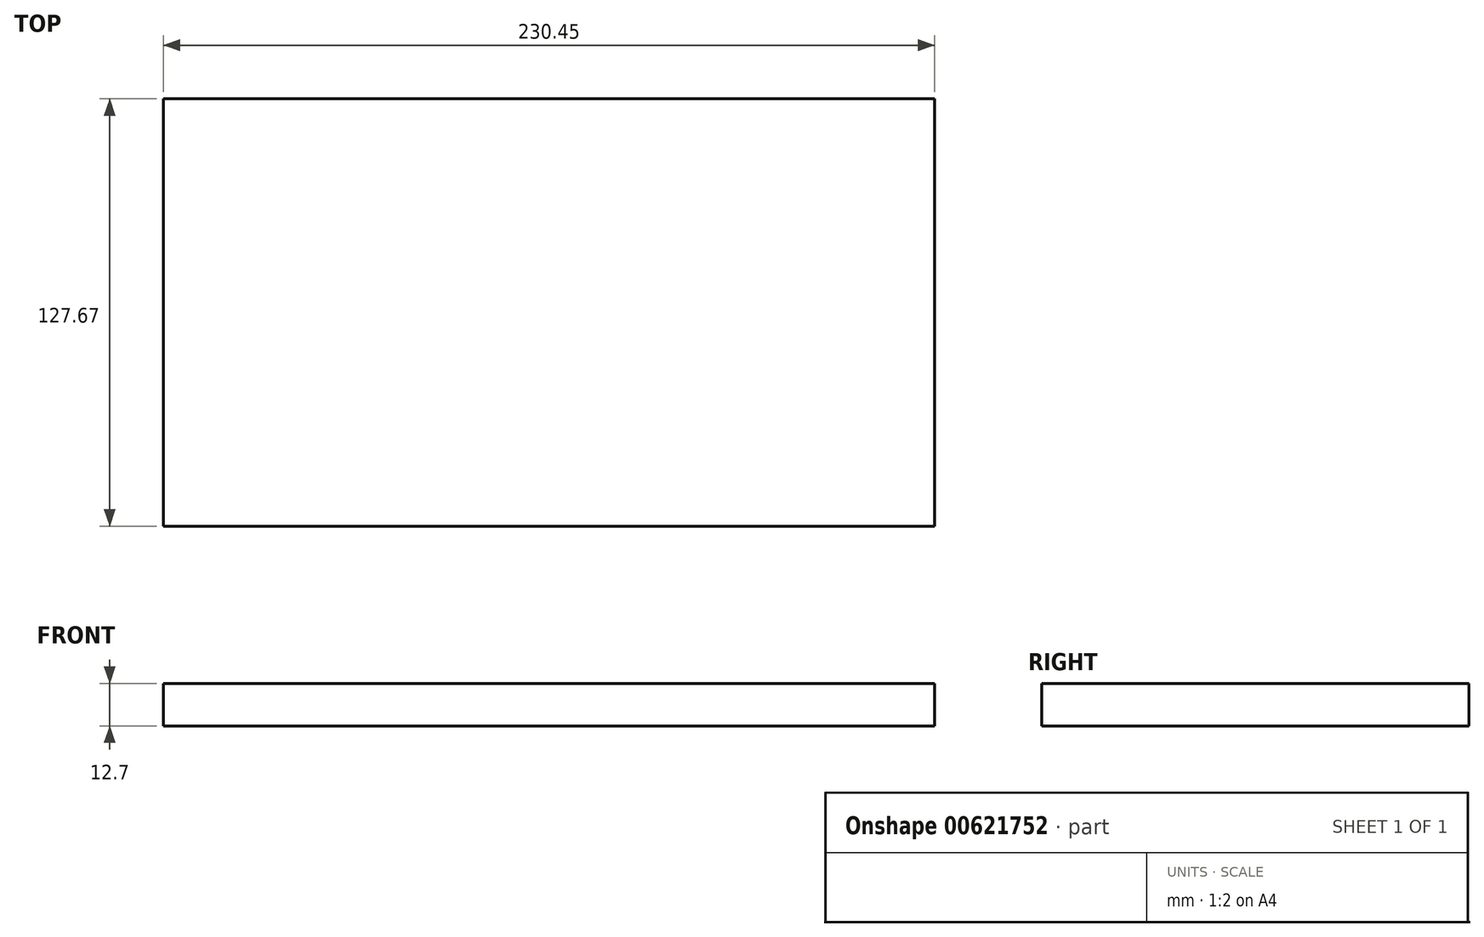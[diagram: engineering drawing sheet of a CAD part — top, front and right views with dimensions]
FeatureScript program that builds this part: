
annotation { "Feature Type Name" : "Feature", "Feature Type Description" : "" }
export const myFeature = defineFeature(function(context is Context, id is Id, definition is map)
    precondition{}
    {
        {
            var Q0;
            Q0=qCreatedBy(makeId("Top.planeOp"),FACE);
            var sketch = newSketch(context, id + "F0", { "sketchPlane" : qUnion([Q0])});
            skLineSegment(sketch, "E0.bottom", {"start": v(-116.26, -63.98) * mm, "end": v(114.2, -63.98) * mm});
            skLineSegment(sketch, "E0.top", {"start": v(-116.26, 63.69) * mm, "end": v(114.2, 63.69) * mm});
            skLineSegment(sketch, "E0.left", {"start": v(-116.26, -63.98) * mm, "end": v(-116.26, 63.69) * mm});
            skLineSegment(sketch, "E0.right", {"start": v(114.2, -63.98) * mm, "end": v(114.2, 63.69) * mm});
            skSolve(sketch);
        }
        {
            var Q0;
            Q0=makeQuery(id+"F0.imprint","IMPRINT",FACE,{"disambiguationData":[TD([[makeQuery(id+"F0.imprint","IMPRINT",EDGE,{"derivedFrom":sQuery(id+"F0.wireOp",EDGE,"E0.bottom")}),1.0]])]});
            extrude(context, id + "F1", {"entities" : qUnion([Q0]), "depth" : 12.7 * mm, "offsetDistance" : 25.4 * mm});
        }
    });
